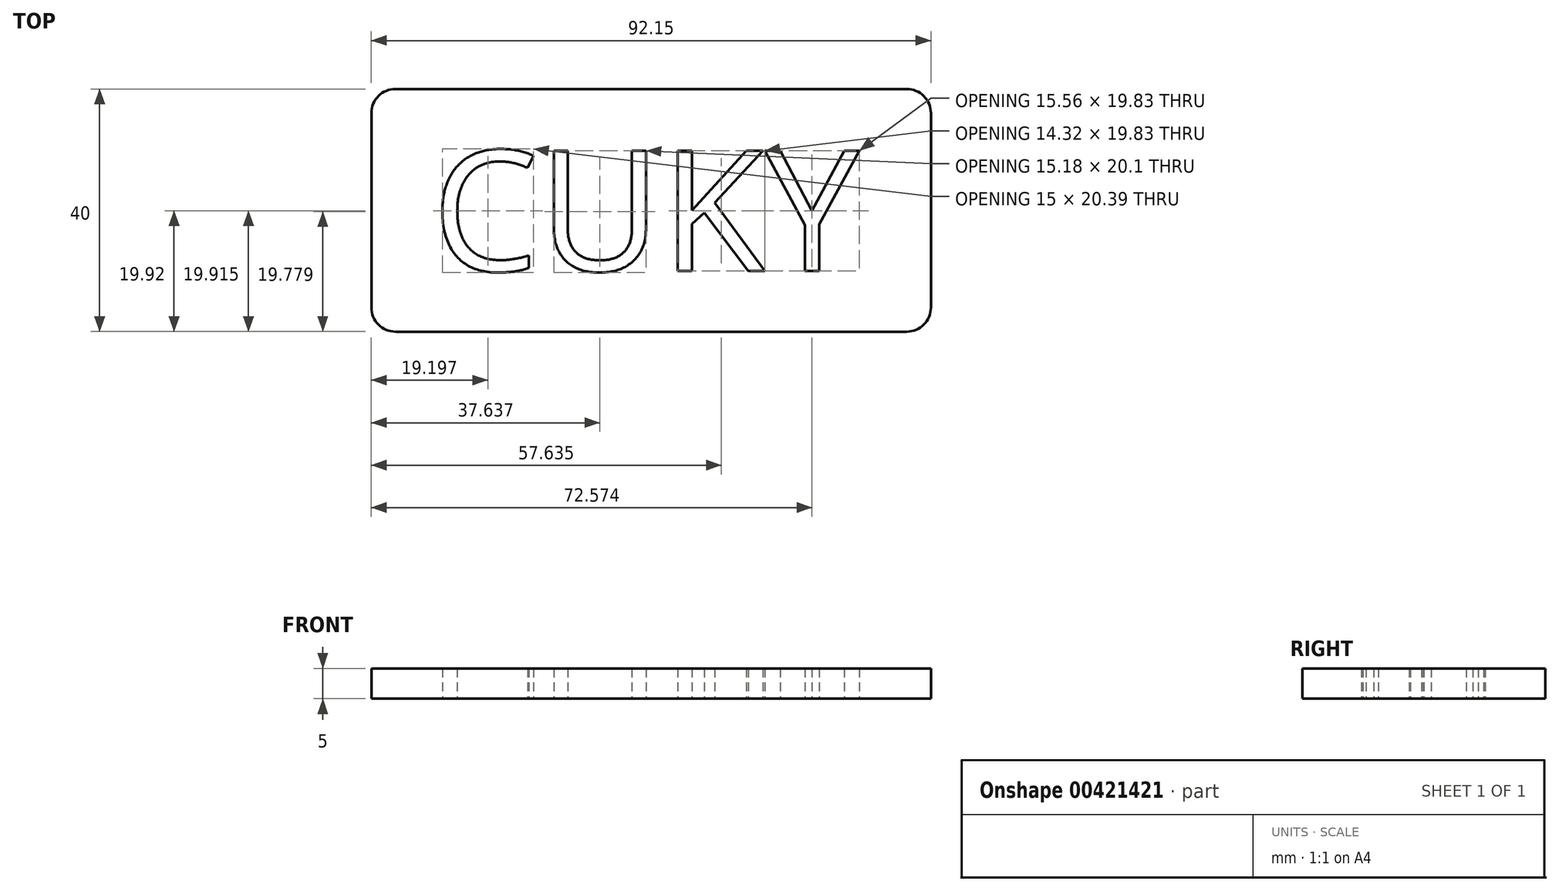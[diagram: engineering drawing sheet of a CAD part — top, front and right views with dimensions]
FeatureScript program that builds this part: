
annotation { "Feature Type Name" : "Feature", "Feature Type Description" : "" }
export const myFeature = defineFeature(function(context is Context, id is Id, definition is map)
    precondition{}
    {
        {
            var Q0;
            Q0=qCreatedBy(makeId("Top.planeOp"),FACE);
            var sketch = newSketch(context, id + "F0", { "sketchPlane" : qUnion([Q0])});
            skText(sketch, "E0", { "text": "CUKY", "fontName": "OpenSans-Regular.ttf"});
            skLineSegment(sketch, "E1.bottom", {"start": v(-79.95, 46.82) * mm, "end": v(12.2, 46.82) * mm});
            skLineSegment(sketch, "E1.top", {"start": v(-79.95, 6.82) * mm, "end": v(12.2, 6.82) * mm});
            skLineSegment(sketch, "E1.left", {"start": v(-79.95, 46.82) * mm, "end": v(-79.95, 6.82) * mm});
            skLineSegment(sketch, "E1.right", {"start": v(12.2, 46.82) * mm, "end": v(12.2, 6.82) * mm});
            const initialGuessF0  = {"E0": [-0.06995, 0.01682, 1, 0, 0.02]};
            skSetInitialGuess(sketch, initialGuessF0);
            skSolve(sketch);
        }
        {
            var Q0;
            Q0=makeQuery(id+"F0.imprint","IMPRINT",FACE,{"disambiguationData":[TD([[makeQuery(id+"F0.imprint","IMPRINT",EDGE,{"derivedFrom":sQuery(id+"F0.wireOp",EDGE,"E0.sketch_text.stroke-0")}),1.0]])]});
            var Q1;
            Q1 = qSketchRegion(id + "F0", true);
            extrude(context, id + "F1", {"entities" : qUnion([Q0, Q1]), "depth" : 5 * mm});
        }
        {
            var Q0;
            Q0=makeQuery(id+"F1.opExtrude","SWEPT_EDGE",EDGE,{"disambiguationData":[OSD([sQuery(id+"F0.wireOp",EDGE,"E1.bottom"),sQuery(id+"F0.wireOp",EDGE,"E1.left")])]});
            var Q1;
            Q1=makeQuery(id+"F1.opExtrude","SWEPT_EDGE",EDGE,{"disambiguationData":[OSD([sQuery(id+"F0.wireOp",EDGE,"E1.top"),sQuery(id+"F0.wireOp",EDGE,"E1.left")])]});
            var Q2;
            Q2=makeQuery(id+"F1.opExtrude","SWEPT_EDGE",EDGE,{"disambiguationData":[OSD([sQuery(id+"F0.wireOp",EDGE,"E1.top"),sQuery(id+"F0.wireOp",EDGE,"E1.right")])]});
            var Q3;
            Q3=makeQuery(id+"F1.opExtrude","SWEPT_EDGE",EDGE,{"disambiguationData":[OSD([sQuery(id+"F0.wireOp",EDGE,"E1.bottom"),sQuery(id+"F0.wireOp",EDGE,"E1.right")])]});
            fillet(context, id + "F2", {"entities" : qUnion([Q0, Q1, Q2, Q3]), "radius" : 4 * mm, "tangentPropagation" : true, "allowEdgeOverflow" : false});
        }
    });
